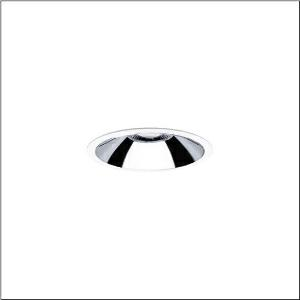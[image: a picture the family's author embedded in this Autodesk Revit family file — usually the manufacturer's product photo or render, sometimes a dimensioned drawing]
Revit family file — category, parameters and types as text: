
# Revit family: lunis_21_l_51db15dd32
name_source: partatom
category: Lighting Fixtures
units: mm (PartAtom-declared; Revit-internal decimal feet)

## family parameters
Cut with Voids When Loaded = No
Host = Face
Light Source = No
Part Type = Normal
Room Calculation Point = No
Round Connector Dimension = Use Diameter
Shared = No

## types (1)
- Lunis 21 L (1 x LED, 1670 lm, 13.8 W, 3000K)
    Apparent Load = 14 VA
    CIE Flux Codes = 90 99 100 100 100
    Color Rendering = 80
    Color Temperature = 3000K
    Default Elevation = 1800 mm
    Description = Lunis 21,  L, downlight, of PC, light emission: direct distribution, LED rated luminous flux: 1.670lm, light colour: 830, control gear: ECG DALI, with terminal, 5-pole, mains connection: 220..240V, AC, housing, round, of diecast aluminium, traffic white (RAL 9016), diameter: 162mm, protection rating (complete): IP20, protection rating (on room side): IP54, insulation class (complete): insulation class II (safety insulation), certification: CE, impact resistance: IK02, packaging unit: 1 piece
    Height = 0 mm  [stored 0 ft]
    Lamp = 1 x LED
    Lamp Light Flux = 1670 lm
    Lamp Power = 13.8 W
    Lamp count = 1
    Length = 162 mm
    Luminous efficacy = 121 lm/W
    Manufacturer = Siteco
    ModVariant = No
    Model = 51DB15DD32
    Mounting Place = Ceiling
    Mounting Type = Recessed
    Number of Poles = 1
    OnlyDefault = Yes
    Power Factor = 1
    Product Name = Lunis 21 L
    Product group = downlight
    ProductGroupID = 400
    Protection Class = Protection class II
    Protection Degree = IP 20
    RLX_Detail_Level = 1
    RLX_Emergency_Light_Flux = 0 lm
    RLX_Emergency_Type = 0
    RLX_Emergency_Type_DB = No
    RlxData = <blob elided: 21217 chars, md5=906b8191>
    Socket = socket
    Standby Power = 0 W
    System Light Flux = 1670 lm
    System Power = 14 W
    Type Comments = Product without accessories
    Type Image = l_1287387.jpg
    URL = http://relux.com
    VarID = ---
    Voltage = 0 V
    Weight = 0.00 kg
    Width = 0 mm  [stored 0 ft]

note: [stored X ft] marks values corroborated as IEEE doubles in the binary element streams (Revit-internal decimal feet)

## geometry (parser evidence)
native form markers: Blend x4, Sweep x10
no freeform markers — native parametric forms only
